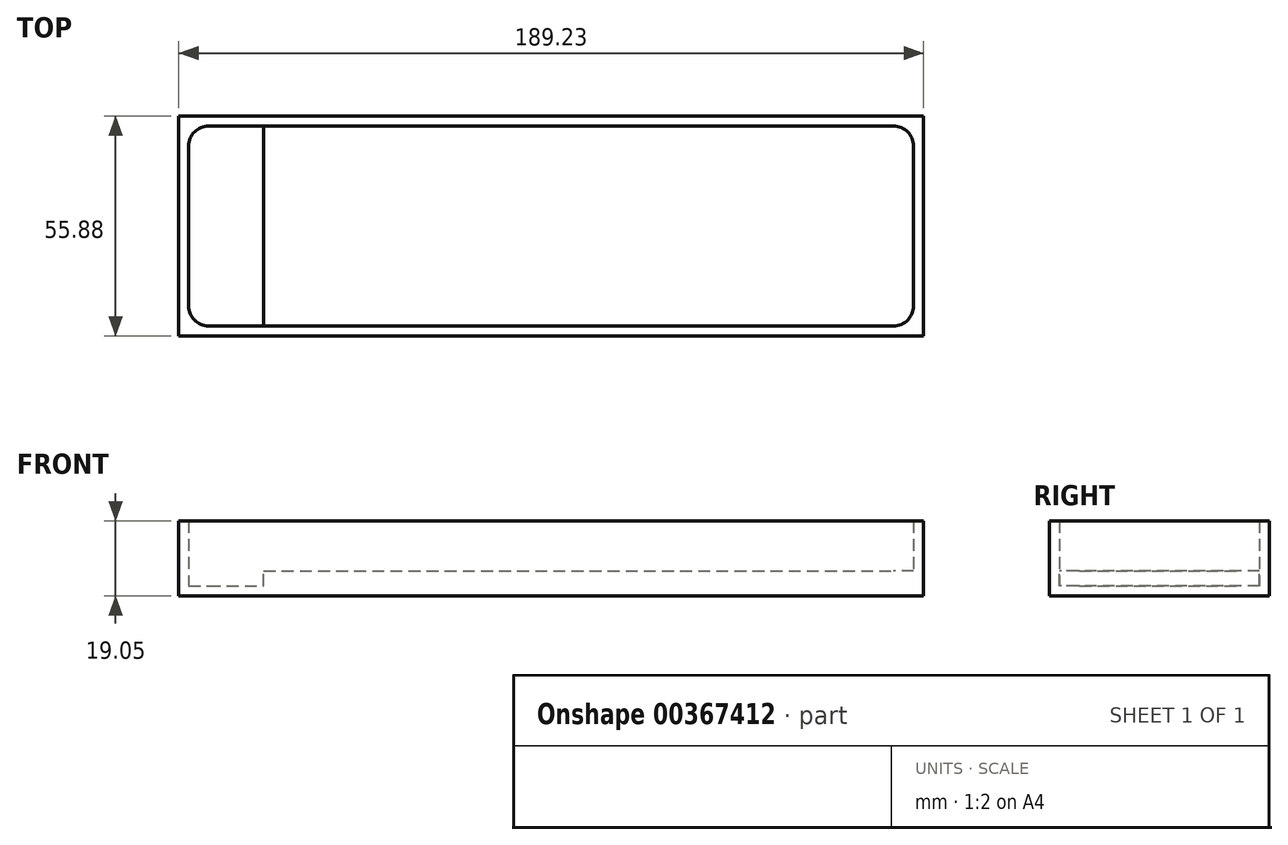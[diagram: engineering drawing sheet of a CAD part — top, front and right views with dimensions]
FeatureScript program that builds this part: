
annotation { "Feature Type Name" : "Feature", "Feature Type Description" : "" }
export const myFeature = defineFeature(function(context is Context, id is Id, definition is map)
    precondition{}
    {
        {
            var Q0;
            Q0=qCreatedBy(makeId("Top.planeOp"),FACE);
            var sketch = newSketch(context, id + "F0", { "sketchPlane" : qUnion([Q0])});
            skLineSegment(sketch, "E0.bottom", {"start": v(0, 0) * mm, "end": v(184.15, 0) * mm});
            skLineSegment(sketch, "E0.top", {"start": v(0, 50.8) * mm, "end": v(184.15, 50.8) * mm});
            skLineSegment(sketch, "E0.left", {"start": v(0, 0) * mm, "end": v(0, 50.8) * mm});
            skLineSegment(sketch, "E0.right", {"start": v(184.15, 0) * mm, "end": v(184.15, 50.8) * mm});
            skLineSegment(sketch, "E1.0", {"start": v(-2.54, 53.34) * mm, "end": v(186.7, 53.34) * mm});
            skLineSegment(sketch, "E1.1", {"start": v(-2.54, -2.54) * mm, "end": v(-2.54, 53.34) * mm});
            skLineSegment(sketch, "E1.2", {"start": v(-2.54, -2.54) * mm, "end": v(186.7, -2.54) * mm});
            skLineSegment(sketch, "E1.3", {"start": v(186.7, -2.54) * mm, "end": v(186.7, 53.34) * mm});
            skSolve(sketch);
        }
        {
            var Q0;
            Q0 = qSketchRegion(id + "F0", true);
            extrude(context, id + "F1", {"entities" : qUnion([Q0]), "depth" : 12.7 * mm});
        }
        {
            var Q0;
            Q0=makeQuery(id+"F1.opExtrude","CAP_FACE",FACE,{"disambiguationData":[OSD([sQuery(id+"F0.wireOp",EDGE,"E0.bottom"),sQuery(id+"F0.wireOp",EDGE,"E0.top"),sQuery(id+"F0.wireOp",EDGE,"E0.left"),sQuery(id+"F0.wireOp",EDGE,"E0.right"),sQuery(id+"F0.wireOp",EDGE,"E1.0"),sQuery(id+"F0.wireOp",EDGE,"E1.1"),sQuery(id+"F0.wireOp",EDGE,"E1.2"),sQuery(id+"F0.wireOp",EDGE,"E1.3")])],"isStart":true});
            var sketch = newSketch(context, id + "F2", { "sketchPlane" : qUnion([Q0])});
            skLineSegment(sketch, "E2.bottom", {"start": v(-2.54, 2.54) * mm, "end": v(186.7, 2.54) * mm});
            skLineSegment(sketch, "E2.top", {"start": v(-2.54, -53.34) * mm, "end": v(186.7, -53.34) * mm});
            skLineSegment(sketch, "E2.left", {"start": v(-2.54, 2.54) * mm, "end": v(-2.54, -53.34) * mm});
            skLineSegment(sketch, "E2.right", {"start": v(186.7, 2.54) * mm, "end": v(186.7, -53.34) * mm});
            skSolve(sketch);
        }
        {
            var Q0;
            Q0 = qSketchRegion(id + "F2", true);
            extrude(context, id + "F3", {"entities" : qUnion([Q0]), "operationType" : NewBodyOperationType.ADD, "depth" : 6.35 * mm});
        }
        {
            var Q0;
            Q0=makeQuery(id+"F3.opExtrude","CAP_FACE",FACE,{"disambiguationData":[OSD([sQuery(id+"F2.wireOp",EDGE,"E2.bottom"),sQuery(id+"F2.wireOp",EDGE,"E2.top"),sQuery(id+"F2.wireOp",EDGE,"E2.left"),sQuery(id+"F2.wireOp",EDGE,"E2.right")])],"isStart":true});
            var sketch = newSketch(context, id + "F4", { "sketchPlane" : qUnion([Q0])});
            skLineSegment(sketch, "E3.bottom", {"start": v(0, 50.8) * mm, "end": v(19.05, 50.8) * mm});
            skLineSegment(sketch, "E3.top", {"start": v(0, 0) * mm, "end": v(19.05, 0) * mm});
            skLineSegment(sketch, "E3.left", {"start": v(0, 50.8) * mm, "end": v(0, 0) * mm});
            skLineSegment(sketch, "E3.right", {"start": v(19.05, 50.8) * mm, "end": v(19.05, 0) * mm});
            skSolve(sketch);
        }
        {
            var Q0;
            Q0 = qSketchRegion(id + "F4", true);
            extrude(context, id + "F5", {"entities" : qUnion([Q0]), "operationType" : NewBodyOperationType.REMOVE, "oppositeDirection" : true, "depth" : 3.8 * mm});
        }
        {
            var Q0;
            Q0=makeQuery(id+"F1.opExtrude","CAP_EDGE",EDGE,{"disambiguationData":[OSD([sQuery(id+"F0.wireOp",EDGE,"E0.top")])],"isStart":true});
            var Q1;
            Q1=makeQuery(id+"F5.boolean.opBoolean","MERGE",EDGE,{"derivedFrom":[makeQuery(id+"F1.opExtrude","SWEPT_EDGE",EDGE,{"disambiguationData":[OSD([sQuery(id+"F0.wireOp",EDGE,"E0.top"),sQuery(id+"F0.wireOp",EDGE,"E0.left")])]}),makeQuery(id+"F5.opExtrude","SWEPT_EDGE",EDGE,{"disambiguationData":[OSD([sQuery(id+"F4.wireOp",EDGE,"E3.bottom"),sQuery(id+"F4.wireOp",EDGE,"E3.left")])]})]});
            var Q2;
            Q2=makeQuery(id+"F1.opExtrude","SWEPT_EDGE",EDGE,{"disambiguationData":[OSD([sQuery(id+"F0.wireOp",EDGE,"E0.top"),sQuery(id+"F0.wireOp",EDGE,"E0.right")])]});
            var Q3;
            Q3=makeQuery(id+"F1.opExtrude","CAP_EDGE",EDGE,{"disambiguationData":[OSD([sQuery(id+"F0.wireOp",EDGE,"E0.right")])],"isStart":true});
            var Q4;
            Q4=makeQuery(id+"F1.opExtrude","SWEPT_EDGE",EDGE,{"disambiguationData":[OSD([sQuery(id+"F0.wireOp",EDGE,"E0.bottom"),sQuery(id+"F0.wireOp",EDGE,"E0.right")])]});
            var Q5;
            Q5=makeQuery(id+"F1.opExtrude","CAP_EDGE",EDGE,{"disambiguationData":[OSD([sQuery(id+"F0.wireOp",EDGE,"E0.bottom")])],"isStart":true});
            var Q6;
            Q6=makeQuery(id+"F5.boolean.opBoolean","MERGE",EDGE,{"derivedFrom":[makeQuery(id+"F1.opExtrude","SWEPT_EDGE",EDGE,{"disambiguationData":[OSD([sQuery(id+"F0.wireOp",EDGE,"E0.bottom"),sQuery(id+"F0.wireOp",EDGE,"E0.left")])]}),makeQuery(id+"F5.opExtrude","SWEPT_EDGE",EDGE,{"disambiguationData":[OSD([sQuery(id+"F4.wireOp",EDGE,"E3.top"),sQuery(id+"F4.wireOp",EDGE,"E3.left")])]})]});
            fillet(context, id + "F6", {"entities" : qUnion([Q0, Q1, Q2, Q3, Q4, Q5, Q6]), "radius" : 5.08 * mm, "tangentPropagation" : true, "allowEdgeOverflow" : false});
        }
    });
